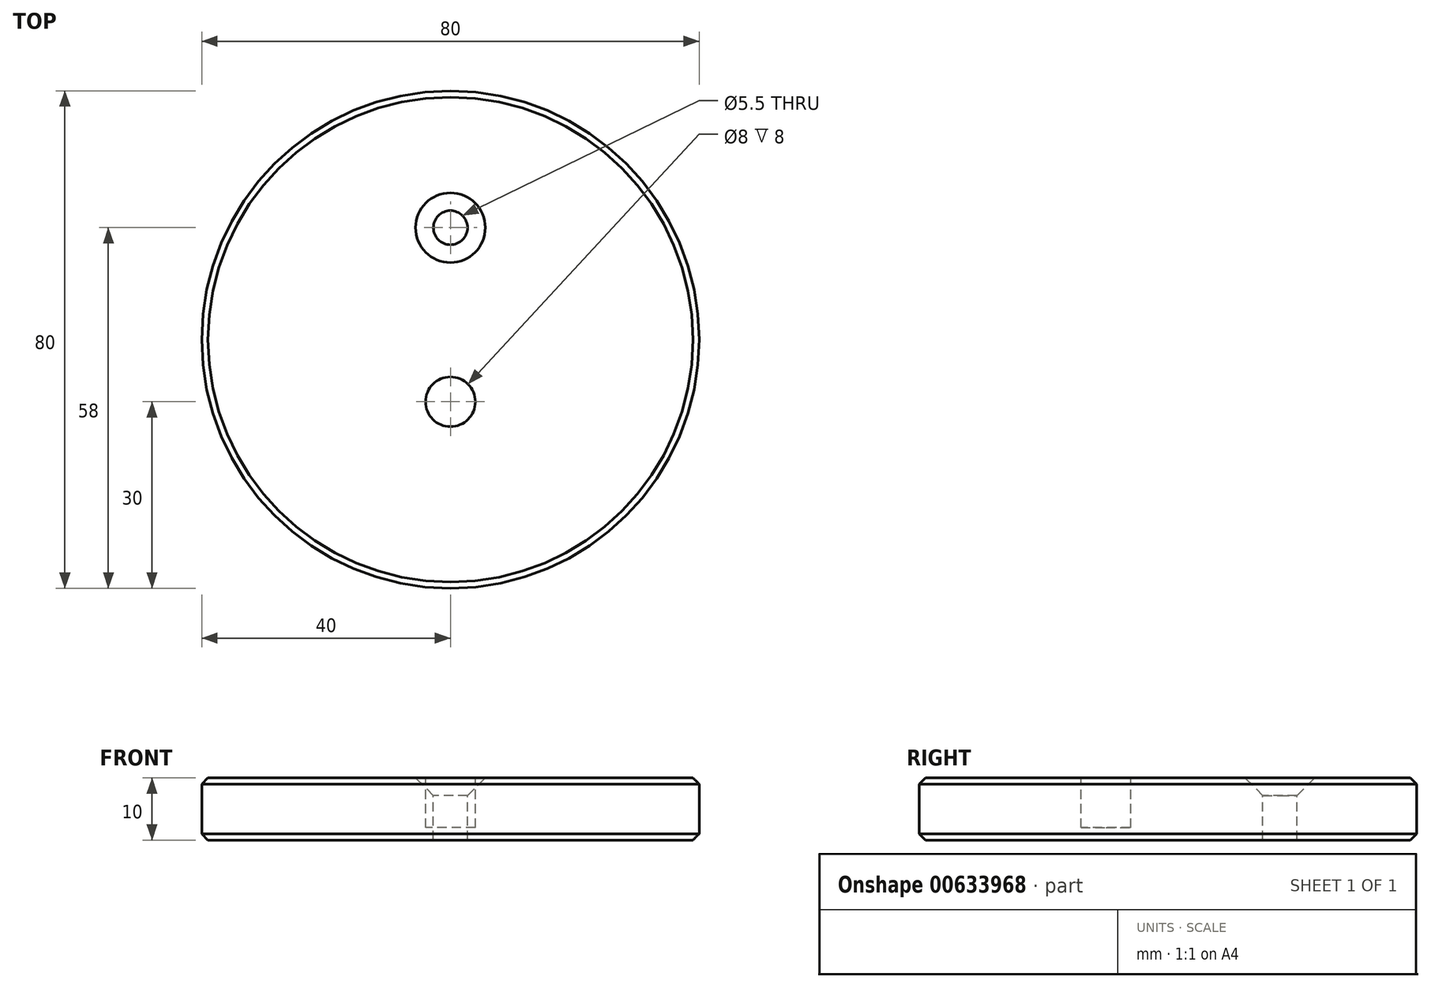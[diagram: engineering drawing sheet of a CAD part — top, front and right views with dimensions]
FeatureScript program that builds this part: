
annotation { "Feature Type Name" : "Feature", "Feature Type Description" : "" }
export const myFeature = defineFeature(function(context is Context, id is Id, definition is map)
    precondition{}
    {
        {
            var Q0;
            Q0=qCreatedBy(makeId("Top.planeOp"),FACE);
            var sketch = newSketch(context, id + "F0", { "sketchPlane" : qUnion([Q0])});
            skCircle(sketch, "E0", {"center": v(0, 0) * mm, "radius": 40 * mm});
            skLineSegment(sketch, "E1", {"start": v(0, 0) * mm, "end": v(0, 18) * mm, "construction": true});
            skPoint(sketch, "E2", {"position": v(0, 18) * mm});
            skSolve(sketch);
        }
        {
            var Q0;
            Q0=qCreatedBy(makeId("Right.planeOp"),FACE);
            var sketch = newSketch(context, id + "F1", { "sketchPlane" : qUnion([Q0])});
            skLineSegment(sketch, "E3", {"start": v(0, 0) * mm, "end": v(0, 53.42) * mm, "construction": true});
            skSolve(sketch);
        }
        {
            var Q0;
            Q0=makeQuery(id+"F0.imprint","IMPRINT",FACE,{"disambiguationData":[TD([[makeQuery(id+"F0.imprint","IMPRINT",EDGE,{"derivedFrom":sQuery(id+"F0.wireOp",EDGE,"E0")}),1.0]])]});
            extrude(context, id + "F2", {"entities" : qUnion([Q0]), "oppositeDirection" : true, "depth" : 10 * mm, "offsetDistance" : 25 * mm});
        }
        {
            var Q0;
            Q0=sQuery(id+"F0.wireOp",VERTEX,"E2");
            var Q1;
            Q1=makeQuery(id+"F2.opExtrude","SWEPT_BODY",BODY,{"disambiguationData":[OSD([sQuery(id+"F0.wireOp",EDGE,"E0")])]});
            hole(context, id + "F3", {"style" : HoleStyle.C_SINK, "endStyle" : HoleEndStyle.THROUGH, "standardTappedOrClearance" : lookupTablePath({ "standard" : "ISO", "fit" : "Normal", "size" : "M5", "type" : "Clearance" }), "standardBlindInLast" : lookupTablePath({ "fit" : "Standard", "standard" : "ISO", "size" : "M5", "type" : "Clearance" }), "holeDiameter" : 5.5 * mm, "cSinkDiameter" : 11.2 * mm, "cSinkAngle" : 90 * degree, "majorDiameter" : 5 * mm, "isTappedThrough" : true, "tappedDepth" : 12 * mm, "tapClearance" : 3, "locations" : qUnion([Q0]), "scope" : qUnion([Q1])});
        }
        {
            var Q0;
            Q0=makeQuery(id+"F0.imprint","IMPRINT",FACE,{"disambiguationData":[TD([[makeQuery(id+"F0.imprint","IMPRINT",EDGE,{"derivedFrom":sQuery(id+"F0.wireOp",EDGE,"E0")}),1.0]])]});
            var sketch = newSketch(context, id + "F4", { "sketchPlane" : qUnion([Q0])});
            skLineSegment(sketch, "E4", {"start": v(0, 0) * mm, "end": v(0, -10) * mm, "construction": true});
            skCircle(sketch, "E5", {"center": v(0, -10) * mm, "radius": 4 * mm});
            skCircle(sketch, "E6", {"center": v(0, 0) * mm, "radius": 14.75 * mm});
            skSolve(sketch);
        }
        {
            var Q0;
            Q0=makeQuery(id+"F4.imprint","IMPRINT",FACE,{"disambiguationData":[TD([[makeQuery(id+"F4.imprint","IMPRINT",EDGE,{"derivedFrom":sQuery(id+"F4.wireOp",EDGE,"E5")}),1.0]])]});
            extrude(context, id + "F5", {"entities" : qUnion([Q0]), "operationType" : NewBodyOperationType.REMOVE, "oppositeDirection" : true, "depth" : 8 * mm, "offsetDistance" : 25 * mm});
        }
        {
            var Q0;
            Q0=makeQuery(id+"FMlGAOC71inLx1z_1.1.F5.boolean.opBoolean","COPY",EDGE,{"derivedFrom":makeQuery(id+"FMlGAOC71inLx1z_1.1.F5.opExtrude","CAP_EDGE",EDGE,{"disambiguationData":[OSD([sQuery(id+"F4.wireOp",EDGE,"RMnRTPDj-t2ow-WKWk-w2nX-JK2CZ0pTL3Rk")])],"isStart":true})});
            var Q1;
            Q1=makeQuery(id+"F5.boolean.opBoolean","COPY",EDGE,{"derivedFrom":makeQuery(id+"F5.opExtrude","CAP_EDGE",EDGE,{"disambiguationData":[OSD([sQuery(id+"F4.wireOp",EDGE,"RMnRTPDj-t2ow-WKWk-w2nX-JK2CZ0pTL3Rk")])],"isStart":true})});
            var Q2;
            Q2=makeQuery(id+"FMlGAOC71inLx1z_1.2.F5.boolean.opBoolean","COPY",EDGE,{"derivedFrom":makeQuery(id+"FMlGAOC71inLx1z_1.2.F5.opExtrude","CAP_EDGE",EDGE,{"disambiguationData":[OSD([sQuery(id+"F4.wireOp",EDGE,"RMnRTPDj-t2ow-WKWk-w2nX-JK2CZ0pTL3Rk")])],"isStart":true})});
            var Q3;
            Q3=makeQuery(id+"F2.opExtrude","CAP_EDGE",EDGE,{"disambiguationData":[OSD([sQuery(id+"F0.wireOp",EDGE,"E0")])],"isStart":false});
            var Q4;
            Q4=makeQuery(id+"F2.opExtrude","CAP_EDGE",EDGE,{"disambiguationData":[OSD([sQuery(id+"F0.wireOp",EDGE,"E0")])],"isStart":true});
            var Q5;
            Q5=makeQuery(id+"F5.boolean.opBoolean","COPY",EDGE,{"derivedFrom":makeQuery(id+"F5.opExtrude","CAP_EDGE",EDGE,{"disambiguationData":[OSD([sQuery(id+"F4.wireOp",EDGE,"E5")])],"isStart":true})});
            var Q6;
            Q6=makeQuery(id+"FMlGAOC71inLx1z_1.2.F5.boolean.opBoolean","COPY",EDGE,{"derivedFrom":makeQuery(id+"FMlGAOC71inLx1z_1.2.F5.opExtrude","CAP_EDGE",EDGE,{"disambiguationData":[OSD([sQuery(id+"F4.wireOp",EDGE,"E5")])],"isStart":true})});
            var Q7;
            Q7=makeQuery(id+"FMlGAOC71inLx1z_1.1.F5.boolean.opBoolean","COPY",EDGE,{"derivedFrom":makeQuery(id+"FMlGAOC71inLx1z_1.1.F5.opExtrude","CAP_EDGE",EDGE,{"disambiguationData":[OSD([sQuery(id+"F4.wireOp",EDGE,"E5")])],"isStart":true})});
            chamfer(context, id + "F6", {"entities" : qUnion([Q0, Q1, Q2, Q3, Q4, Q5, Q6, Q7]), "width" : 1 * mm, "tangentPropagation" : true});
        }
    });
